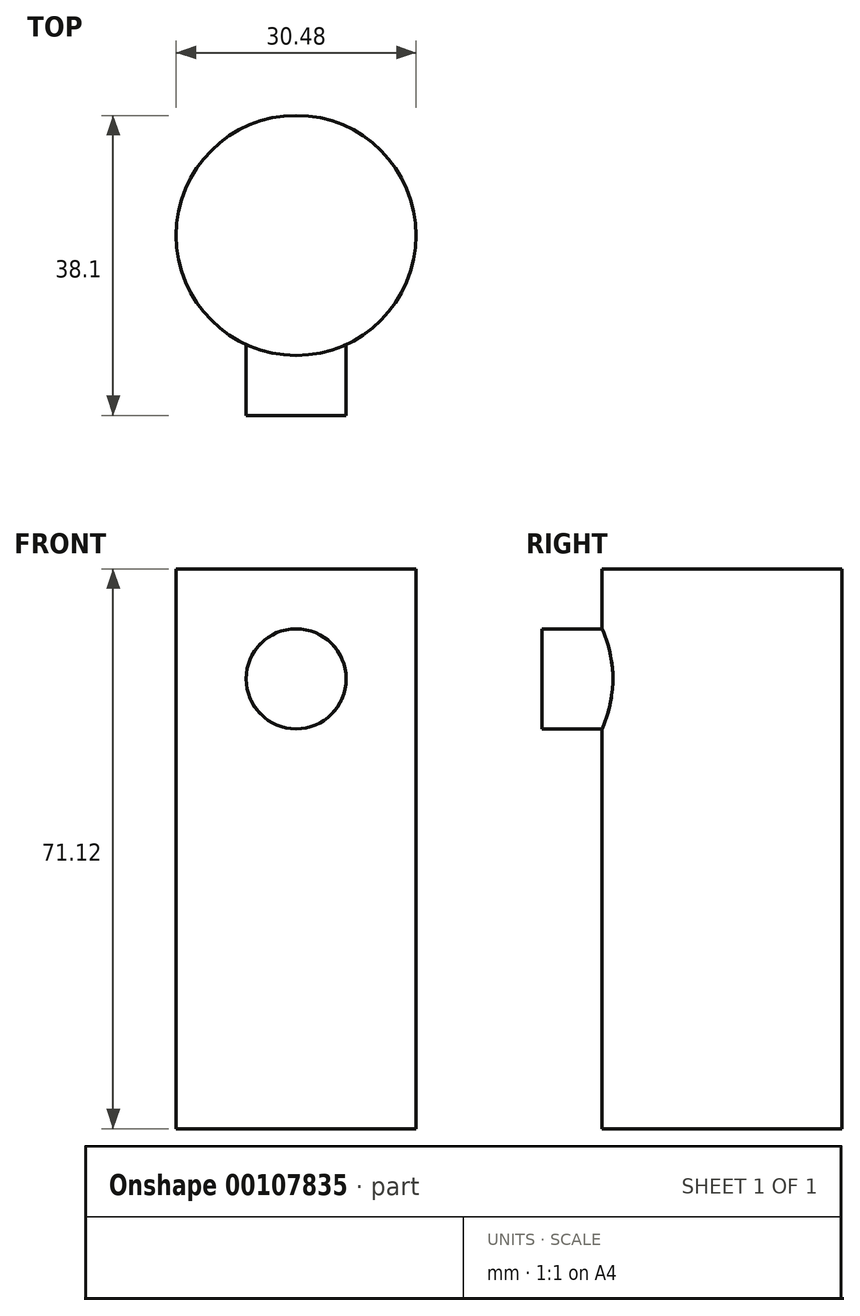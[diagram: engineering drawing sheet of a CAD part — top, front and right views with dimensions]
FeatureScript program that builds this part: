
annotation { "Feature Type Name" : "Feature", "Feature Type Description" : "" }
export const myFeature = defineFeature(function(context is Context, id is Id, definition is map)
    precondition{}
    {
        {
            var Q0;
            Q0=qCreatedBy(makeId("Top.planeOp"),FACE);
            var sketch = newSketch(context, id + "F0", { "sketchPlane" : qUnion([Q0])});
            skCircle(sketch, "E0", {"center": v(0, 0) * mm, "radius": 15.24 * mm});
            skSolve(sketch);
        }
        {
            var Q0;
            Q0 = qSketchRegion(id + "F0", true);
            extrude(context, id + "F1", {"entities" : qUnion([Q0]), "depth" : 71.12 * mm});
        }
        {
            var Q0;
            Q0=qCreatedBy(makeId("Front.planeOp"),FACE);
            var sketch = newSketch(context, id + "F2", { "sketchPlane" : qUnion([Q0])});
            skCircle(sketch, "E1", {"center": v(0, 57.15) * mm, "radius": 6.35 * mm});
            skSolve(sketch);
        }
        {
            var Q0;
            Q0 = qSketchRegion(id + "F2", true);
            extrude(context, id + "F3", {"entities" : qUnion([Q0]), "operationType" : NewBodyOperationType.ADD, "depth" : 22.86 * mm});
        }
    });
